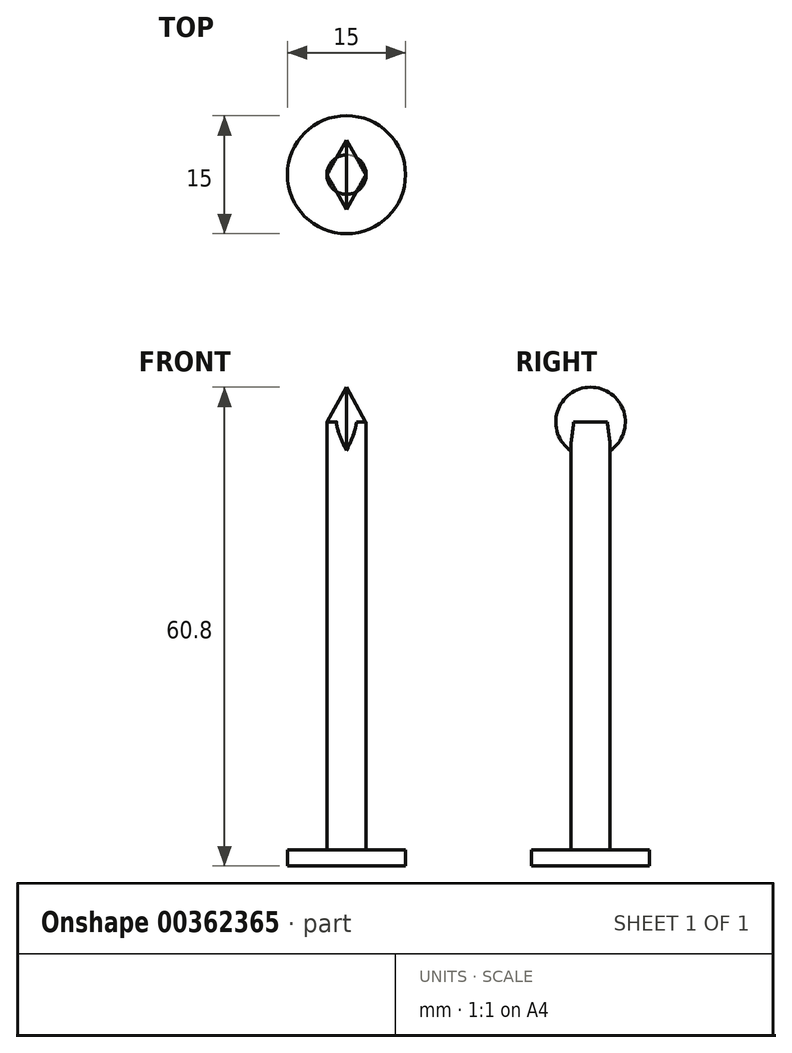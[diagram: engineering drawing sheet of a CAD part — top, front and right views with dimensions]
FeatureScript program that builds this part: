
annotation { "Feature Type Name" : "Feature", "Feature Type Description" : "" }
export const myFeature = defineFeature(function(context is Context, id is Id, definition is map)
    precondition{}
    {
        {
            var Q0;
            Q0=qCreatedBy(makeId("Top.planeOp"),FACE);
            var sketch = newSketch(context, id + "F0", { "sketchPlane" : qUnion([Q0])});
            skCircle(sketch, "E0", {"center": v(0, 0) * mm, "radius": 7.5 * mm});
            skSolve(sketch);
        }
        {
            var Q0;
            Q0=makeQuery(id+"F0.imprint","IMPRINT",FACE,{"disambiguationData":[TD([[makeQuery(id+"F0.imprint","IMPRINT",EDGE,{"derivedFrom":sQuery(id+"F0.wireOp",EDGE,"E0")}),1.0]])]});
            extrude(context, id + "F1", {"entities" : qUnion([Q0]), "depth" : 2 * mm});
        }
        {
            var Q0;
            Q0=qCreatedBy(makeId("Top.planeOp"),FACE);
            var sketch = newSketch(context, id + "F2", { "sketchPlane" : qUnion([Q0])});
            skCircle(sketch, "E1", {"center": v(0, 0) * mm, "radius": 2.5 * mm});
            skSolve(sketch);
        }
        {
            var Q0;
            Q0 = qSketchRegion(id + "F2", true);
            extrude(context, id + "F3", {"entities" : qUnion([Q0]), "operationType" : NewBodyOperationType.ADD, "depth" : 56.4 * mm});
        }
        {
            var Q0;
            Q0=qCreatedBy(makeId("Front.planeOp"),FACE);
            var sketch = newSketch(context, id + "F4", { "sketchPlane" : qUnion([Q0])});
            skLineSegment(sketch, "E2", {"start": v(0, 56.38) * mm, "end": v(2.45, 56.38) * mm});
            skLineSegment(sketch, "E3", {"start": v(2.45, 56.38) * mm, "end": v(0, 60.8) * mm});
            skLineSegment(sketch, "E4", {"start": v(0, 60.8) * mm, "end": v(-2.47, 56.38) * mm});
            skLineSegment(sketch, "E5", {"start": v(-2.47, 56.38) * mm, "end": v(0, 56.38) * mm});
            skSolve(sketch);
        }
        {
            var Q0;
            Q0=makeQuery(id+"F4.imprint","IMPRINT",FACE,{"disambiguationData":[TD([[makeQuery(id+"F4.imprint","IMPRINT",EDGE,{"derivedFrom":sQuery(id+"F4.wireOp",EDGE,"E2")}),1.0]])]});
            var Q1;
            Q1=sQuery(id+"F4.wireOp",EDGE,"E2");
            revolve(context, id + "F5", {"operationType" : NewBodyOperationType.ADD, "entities" : qUnion([Q0]), "axis" : qUnion([Q1]), "revolveType" : RevolveType.FULL});
        }
    });
